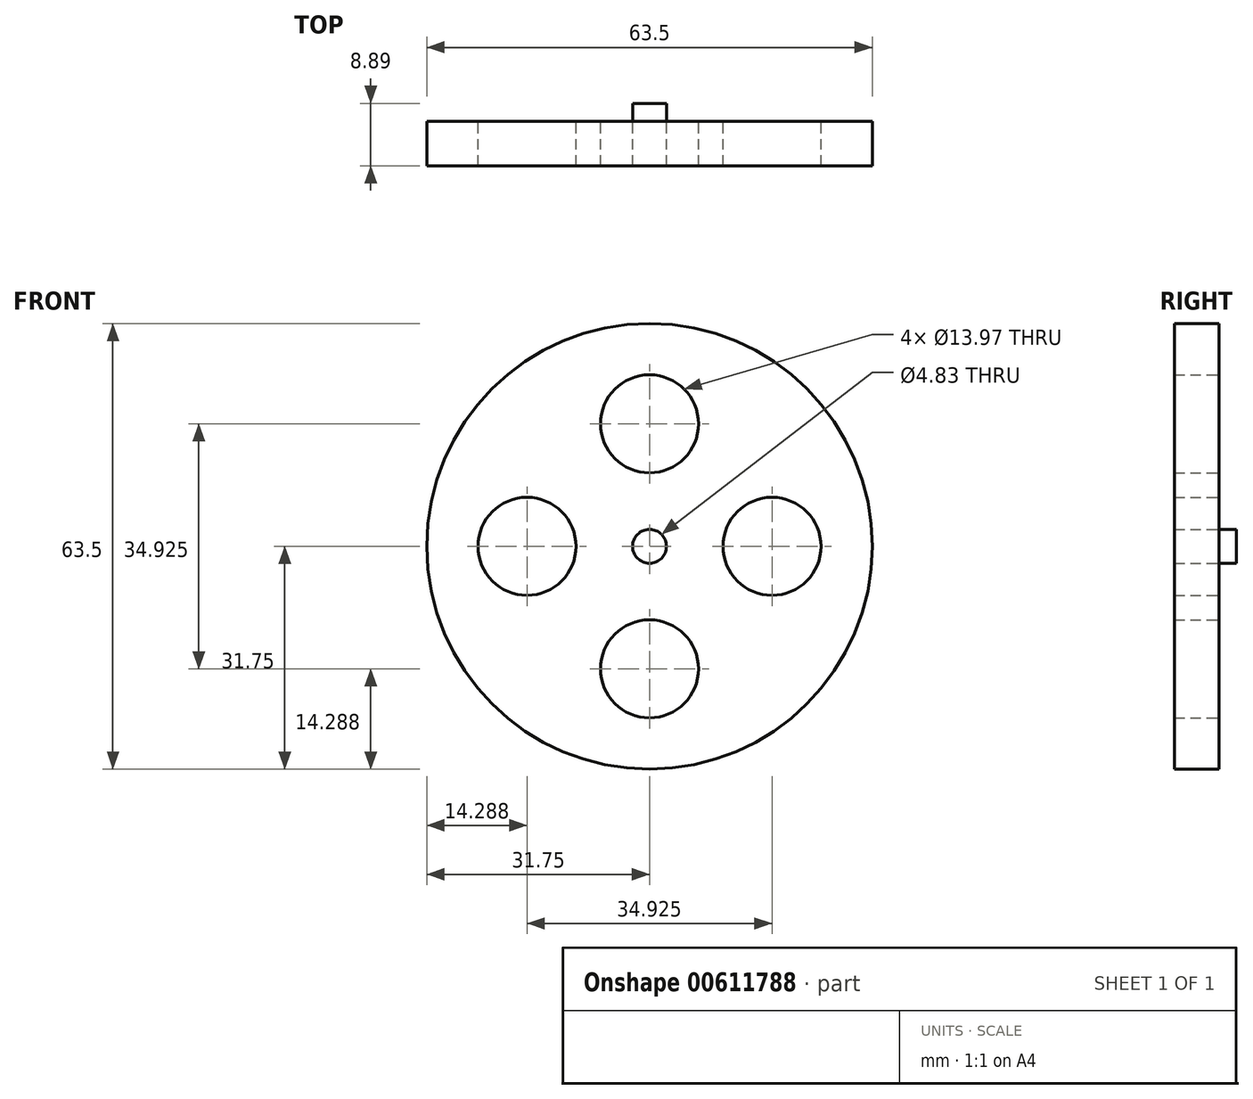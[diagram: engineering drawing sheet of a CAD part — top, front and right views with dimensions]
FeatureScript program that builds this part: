
annotation { "Feature Type Name" : "Feature", "Feature Type Description" : "" }
export const myFeature = defineFeature(function(context is Context, id is Id, definition is map)
    precondition{}
    {
        {
            var Q0;
            Q0=qCreatedBy(makeId("Front.planeOp"),FACE);
            var sketch = newSketch(context, id + "F0", { "sketchPlane" : qUnion([Q0])});
            skCircle(sketch, "E0", {"center": v(0, 0) * mm, "radius": 31.75 * mm});
            skCircle(sketch, "E1", {"center": v(0, 0) * mm, "radius": 2.41 * mm});
            skCircle(sketch, "E2", {"center": v(0, -17.46) * mm, "radius": 6.99 * mm});
            skCircle(sketch, "E3.1.0", {"center": v(17.46, 0) * mm, "radius": 6.99 * mm});
            skCircle(sketch, "E3.2.0", {"center": v(0, 17.46) * mm, "radius": 6.99 * mm});
            skCircle(sketch, "E3.3.0", {"center": v(-17.46, 0) * mm, "radius": 6.99 * mm});
            skSolve(sketch);
        }
        {
            var Q0;
            Q0 = qSketchRegion(id + "F0", true);
            extrude(context, id + "F1", {"entities" : qUnion([Q0]), "depth" : 6.35 * mm, "offsetDistance" : 25.4 * mm});
        }
        {
            var Q0;
            Q0=makeQuery(id+"F0.imprint","IMPRINT",FACE,{"disambiguationData":[TD([[makeQuery(id+"F0.imprint","IMPRINT",EDGE,{"derivedFrom":sQuery(id+"F0.wireOp",EDGE,"E1")}),1.0]])]});
            extrude(context, id + "F2", {"entities" : qUnion([Q0]), "oppositeDirection" : true, "depth" : 2.54 * mm, "offsetDistance" : 25.4 * mm});
        }
    });
